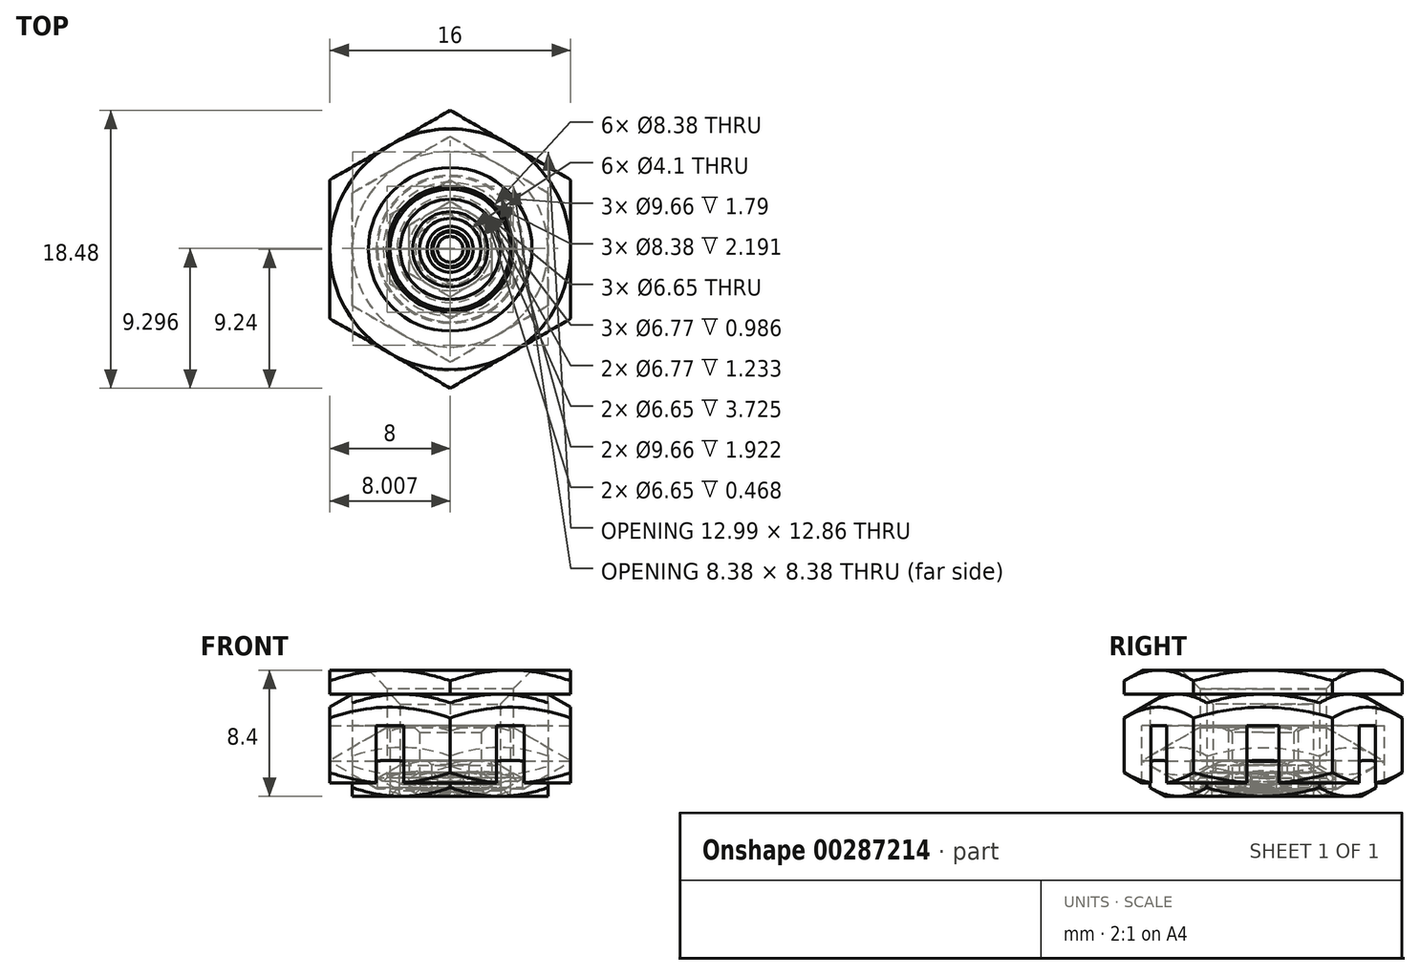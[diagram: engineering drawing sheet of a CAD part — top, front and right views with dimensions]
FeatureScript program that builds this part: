
annotation { "Feature Type Name" : "Feature", "Feature Type Description" : "" }
export const myFeature = defineFeature(function(context is Context, id is Id, definition is map)
    precondition{}
    {
        {
            var Q0;
            Q0=qCreatedBy(makeId("Top.planeOp"),FACE);
            var sketch = newSketch(context, id + "F0", { "sketchPlane" : qUnion([Q0])});
            skCircle(sketch, "E0.cCircle", {"center": v(0, 0) * mm, "radius": 8 * mm, "construction": true});
            skLineSegment(sketch, "E0.0", {"start": v(8, 4.62) * mm, "end": v(8, -4.62) * mm});
            skLineSegment(sketch, "E0.1", {"start": v(8, -4.62) * mm, "end": v(0, -9.24) * mm});
            skLineSegment(sketch, "E0.2", {"start": v(0, -9.24) * mm, "end": v(-8, -4.62) * mm});
            skLineSegment(sketch, "E0.3", {"start": v(-8, -4.62) * mm, "end": v(-8, 4.62) * mm});
            skLineSegment(sketch, "E0.4", {"start": v(-8, 4.62) * mm, "end": v(0, 9.24) * mm});
            skLineSegment(sketch, "E0.5", {"start": v(0, 9.24) * mm, "end": v(8, 4.62) * mm});
            skPoint(sketch, "E0.0.midPoint", {"position": v(8, 0) * mm});
            skCircle(sketch, "E1", {"center": v(0, 0) * mm, "radius": 4.19 * mm});
            skSolve(sketch);
        }
        {
            var Q0;
            Q0=qSketchRegion(id+"F0",true);
            extrude(context, id + "F1", {"entities" : qUnion([Q0]), "depth" : 8.4 * mm});
        }
        {
            var Q0;
            Q0=qCreatedBy(makeId("Front.planeOp"),FACE);
            var sketch = newSketch(context, id + "F2", { "sketchPlane" : qUnion([Q0])});
            skLineSegment(sketch, "E2", {"start": v(0, 0) * mm, "end": v(0, 8.4) * mm, "construction": true});
            skLineSegment(sketch, "E3", {"start": v(0, 4.2) * mm, "end": v(8, 4.2) * mm, "construction": true});
            skLineSegment(sketch, "E4", {"start": v(8, 8.4) * mm, "end": v(15.27, 8.4) * mm});
            skLineSegment(sketch, "E5", {"start": v(15.27, 8.4) * mm, "end": v(15.27, 4.2) * mm});
            skLineSegment(sketch, "E6", {"start": v(15.27, 4.2) * mm, "end": v(8, 8.4) * mm});
            skLineSegment(sketch, "E7.MirrorCS", {"start": v(15.27, 0) * mm, "end": v(15.27, 4.2) * mm});
            skLineSegment(sketch, "E8.MirrorCS", {"start": v(15.27, 4.2) * mm, "end": v(8, 0) * mm});
            skLineSegment(sketch, "E9.MirrorCS", {"start": v(8, 0) * mm, "end": v(15.27, 0) * mm});
            skSolve(sketch);
        }
        {
            var Q0;
            Q0=qSketchRegion(id+"F2",true);
            var Q1;
            Q1=sQuery(id+"F2.wireOp",EDGE,"E2");
            revolve(context, id + "F3", {"operationType" : NewBodyOperationType.REMOVE, "entities" : qUnion([Q0]), "axis" : qUnion([Q1]), "revolveType" : RevolveType.FULL, "oppositeDirection" : true});
        }
        {
            var Q0;
            Q0=makeQuery(id+"F1.opExtrude","SWEPT_FACE",FACE,{"disambiguationData":[OSD([sQuery(id+"F0.wireOp",EDGE,"E1")])]});
            chamfer(context, id + "F4", {"entities" : qUnion([Q0]), "width" : 1.25 * mm, "tangentPropagation" : true});
        }
        {
            var Q0;
            Q0=qCreatedBy(makeId("Top.planeOp"),FACE);
            var sketch = newSketch(context, id + "F5", { "sketchPlane" : qUnion([Q0])});
            skCircle(sketch, "E10.cCircle", {"center": v(0, 0) * mm, "radius": 2.75 * mm, "construction": true});
            skLineSegment(sketch, "E10.0", {"start": v(2.75, 1.59) * mm, "end": v(2.75, -1.59) * mm});
            skLineSegment(sketch, "E10.1", {"start": v(2.75, -1.59) * mm, "end": v(0, -3.18) * mm});
            skLineSegment(sketch, "E10.2", {"start": v(0, -3.18) * mm, "end": v(-2.75, -1.59) * mm});
            skLineSegment(sketch, "E10.3", {"start": v(-2.75, -1.59) * mm, "end": v(-2.75, 1.59) * mm});
            skLineSegment(sketch, "E10.4", {"start": v(-2.75, 1.59) * mm, "end": v(0, 3.18) * mm});
            skLineSegment(sketch, "E10.5", {"start": v(0, 3.18) * mm, "end": v(2.75, 1.59) * mm});
            skPoint(sketch, "E10.0.midPoint", {"position": v(2.75, 0) * mm});
            skCircle(sketch, "E11", {"center": v(0, 0) * mm, "radius": 1.23 * mm});
            skSolve(sketch);
        }
        {
            var Q0;
            Q0=qSketchRegion(id+"F5",true);
            extrude(context, id + "F6", {"entities" : qUnion([Q0]), "depth" : 2.4 * mm});
        }
        {
            var Q0;
            Q0=qCreatedBy(makeId("Front.planeOp"),FACE);
            var sketch = newSketch(context, id + "F7", { "sketchPlane" : qUnion([Q0])});
            skLineSegment(sketch, "E12.0", {"start": v(2.75, 2.4) * mm, "end": v(2.75, 0) * mm, "construction": true});
            skLineSegment(sketch, "E13", {"start": v(2.75, 2.4) * mm, "end": v(4.83, 2.4) * mm});
            skLineSegment(sketch, "E14", {"start": v(4.83, 2.4) * mm, "end": v(4.83, 0) * mm});
            skLineSegment(sketch, "E15", {"start": v(4.83, 0) * mm, "end": v(2.75, 0) * mm});
            skLineSegment(sketch, "E16", {"start": v(2.75, 2.4) * mm, "end": v(4.83, 1.2) * mm});
            skLineSegment(sketch, "E17", {"start": v(4.83, 1.2) * mm, "end": v(2.75, 0) * mm});
            skLineSegment(sketch, "E18", {"start": v(0, 0) * mm, "end": v(0, 2.35) * mm, "construction": true});
            skSolve(sketch);
        }
        {
            var Q0;
            Q0=qSketchRegion(id+"F7",true);
            var Q1;
            Q1=sQuery(id+"F7.wireOp",EDGE,"E18");
            revolve(context, id + "F8", {"operationType" : NewBodyOperationType.REMOVE, "entities" : qUnion([Q0]), "axis" : qUnion([Q1]), "revolveType" : RevolveType.FULL, "oppositeDirection" : true});
        }
        {
            var Q0;
            Q0=makeQuery(id+"F6.opExtrude","SWEPT_FACE",FACE,{"disambiguationData":[OSD([sQuery(id+"F5.wireOp",EDGE,"E11")])]});
            chamfer(context, id + "F9", {"entities" : qUnion([Q0]), "width" : 0.3 * mm, "tangentPropagation" : true});
        }
        {
            var Q0;
            Q0=qCreatedBy(makeId("Top.planeOp"),FACE);
            var sketch = newSketch(context, id + "F10", { "sketchPlane" : qUnion([Q0])});
            skCircle(sketch, "E19.cCircle", {"center": v(0, 0) * mm, "radius": 4 * mm, "construction": true});
            skLineSegment(sketch, "E19.0", {"start": v(4, 2.3) * mm, "end": v(4, -2.3) * mm});
            skLineSegment(sketch, "E19.1", {"start": v(4, -2.3) * mm, "end": v(0, -4.62) * mm});
            skLineSegment(sketch, "E19.2", {"start": v(0, -4.62) * mm, "end": v(-4, -2.3) * mm});
            skLineSegment(sketch, "E19.3", {"start": v(-4, -2.3) * mm, "end": v(-4, 2.3) * mm});
            skLineSegment(sketch, "E19.4", {"start": v(-4, 2.3) * mm, "end": v(0, 4.62) * mm});
            skLineSegment(sketch, "E19.5", {"start": v(0, 4.62) * mm, "end": v(4, 2.3) * mm});
            skPoint(sketch, "E19.0.midPoint", {"position": v(4, 0) * mm});
            skCircle(sketch, "E20", {"center": v(0, 0) * mm, "radius": 2.05 * mm});
            skSolve(sketch);
        }
        {
            var Q0;
            Q0=qSketchRegion(id+"F10",true);
            extrude(context, id + "F11", {"entities" : qUnion([Q0]), "depth" : 4.7 * mm});
        }
        {
            var Q0;
            Q0=qCreatedBy(makeId("Front.planeOp"),FACE);
            var sketch = newSketch(context, id + "F12", { "sketchPlane" : qUnion([Q0])});
            skLineSegment(sketch, "E21.0", {"start": v(-4, 4.7) * mm, "end": v(-4, 0) * mm, "construction": true});
            skLineSegment(sketch, "E22", {"start": v(-4, 4.7) * mm, "end": v(-8.07, 4.7) * mm});
            skLineSegment(sketch, "E23", {"start": v(-8.07, 4.7) * mm, "end": v(-8.07, 0) * mm});
            skLineSegment(sketch, "E24", {"start": v(-8.07, 0) * mm, "end": v(-4, 0) * mm});
            skLineSegment(sketch, "E25", {"start": v(-4, 0) * mm, "end": v(-8.07, 2.35) * mm});
            skLineSegment(sketch, "E26", {"start": v(-8.07, 2.35) * mm, "end": v(-4, 4.7) * mm});
            skLineSegment(sketch, "E27", {"start": v(0, 0) * mm, "end": v(0, 9.38) * mm, "construction": true});
            skSolve(sketch);
        }
        {
            var Q0;
            Q0=qSketchRegion(id+"F12",true);
            var Q1;
            Q1=sQuery(id+"F12.wireOp",EDGE,"E27");
            revolve(context, id + "F13", {"operationType" : NewBodyOperationType.REMOVE, "entities" : qUnion([Q0]), "axis" : qUnion([Q1]), "revolveType" : RevolveType.FULL, "oppositeDirection" : true});
        }
        {
            var Q0;
            Q0=makeQuery(id+"F11.opExtrude","SWEPT_FACE",FACE,{"disambiguationData":[OSD([sQuery(id+"F10.wireOp",EDGE,"E20")])]});
            chamfer(context, id + "F14", {"entities" : qUnion([Q0]), "width" : 0.45 * mm, "tangentPropagation" : true});
        }
        {
            var Q0;
            Q0=qCreatedBy(makeId("Top.planeOp"),FACE);
            var sketch = newSketch(context, id + "F15", { "sketchPlane" : qUnion([Q0])});
            skCircle(sketch, "E28.cCircle", {"center": v(0, 0) * mm, "radius": 6.5 * mm, "construction": true});
            skLineSegment(sketch, "E28.0", {"start": v(6.5, 3.75) * mm, "end": v(6.5, -3.75) * mm});
            skLineSegment(sketch, "E28.1", {"start": v(6.5, -3.75) * mm, "end": v(0, -7.5) * mm});
            skLineSegment(sketch, "E28.2", {"start": v(0, -7.5) * mm, "end": v(-6.5, -3.75) * mm});
            skLineSegment(sketch, "E28.3", {"start": v(-6.5, -3.75) * mm, "end": v(-6.5, 3.75) * mm});
            skLineSegment(sketch, "E28.4", {"start": v(-6.5, 3.75) * mm, "end": v(0, 7.5) * mm});
            skLineSegment(sketch, "E28.5", {"start": v(0, 7.5) * mm, "end": v(6.5, 3.75) * mm});
            skPoint(sketch, "E28.0.midPoint", {"position": v(6.5, 0) * mm});
            skCircle(sketch, "E29", {"center": v(0, 0) * mm, "radius": 3.33 * mm});
            skSolve(sketch);
        }
        {
            var Q0;
            Q0=qSketchRegion(id+"F15",true);
            extrude(context, id + "F16", {"entities" : qUnion([Q0]), "depth" : 6.8 * mm});
        }
        {
            var Q0;
            Q0=qCreatedBy(makeId("Front.planeOp"),FACE);
            var sketch = newSketch(context, id + "F17", { "sketchPlane" : qUnion([Q0])});
            skLineSegment(sketch, "E30.0", {"start": v(6.5, 6.8) * mm, "end": v(6.5, 0) * mm, "construction": true});
            skLineSegment(sketch, "E31", {"start": v(6.5, 6.8) * mm, "end": v(12.39, 6.8) * mm});
            skLineSegment(sketch, "E32", {"start": v(12.39, 6.8) * mm, "end": v(12.39, 0) * mm});
            skLineSegment(sketch, "E33", {"start": v(12.39, 0) * mm, "end": v(6.5, 0) * mm});
            skLineSegment(sketch, "E34", {"start": v(6.5, 0) * mm, "end": v(12.39, 3.4) * mm});
            skLineSegment(sketch, "E35", {"start": v(12.39, 3.4) * mm, "end": v(6.5, 6.8) * mm});
            skLineSegment(sketch, "E36", {"start": v(0, 0) * mm, "end": v(0, 12.87) * mm, "construction": true});
            skSolve(sketch);
        }
        {
            var Q0;
            Q0=qSketchRegion(id+"F17",true);
            var Q1;
            Q1=sQuery(id+"F17.wireOp",EDGE,"E36");
            revolve(context, id + "F18", {"operationType" : NewBodyOperationType.REMOVE, "entities" : qUnion([Q0]), "axis" : qUnion([Q1]), "revolveType" : RevolveType.FULL, "oppositeDirection" : true});
        }
        {
            var Q0;
            Q0=makeQuery(id+"F16.opExtrude","SWEPT_FACE",FACE,{"disambiguationData":[OSD([sQuery(id+"F15.wireOp",EDGE,"E29")])]});
            chamfer(context, id + "F19", {"entities" : qUnion([Q0]), "width" : (1.35 / 2) * mm, "tangentPropagation" : true});
        }
        {
            var Q0;
            Q0=qCreatedBy(makeId("Top.planeOp"),FACE);
            var sketch = newSketch(context, id + "F20", { "sketchPlane" : qUnion([Q0])});
            skCircle(sketch, "E37.cCircle", {"center": v(0, 0) * mm, "radius": 2 * mm, "construction": true});
            skLineSegment(sketch, "E37.0", {"start": v(2, 1.15) * mm, "end": v(2, -1.15) * mm});
            skLineSegment(sketch, "E37.1", {"start": v(2, -1.15) * mm, "end": v(0, -2.3) * mm});
            skLineSegment(sketch, "E37.2", {"start": v(0, -2.3) * mm, "end": v(-2, -1.15) * mm});
            skLineSegment(sketch, "E37.3", {"start": v(-2, -1.15) * mm, "end": v(-2, 1.15) * mm});
            skLineSegment(sketch, "E37.4", {"start": v(-2, 1.15) * mm, "end": v(0, 2.3) * mm});
            skLineSegment(sketch, "E37.5", {"start": v(0, 2.3) * mm, "end": v(2, 1.15) * mm});
            skPoint(sketch, "E37.0.midPoint", {"position": v(2, 0) * mm});
            skCircle(sketch, "E38", {"center": v(0, 0) * mm, "radius": 0.85 * mm});
            skSolve(sketch);
        }
        {
            var Q0;
            Q0 = qSketchRegion(id + "F20", true);
            extrude(context, id + "F21", {"entities" : qUnion([Q0]), "depth" : 1.6 * mm, "offsetDistance" : 25 * mm});
        }
        {
            var Q0;
            Q0=qCreatedBy(makeId("Front.planeOp"),FACE);
            var sketch = newSketch(context, id + "F22", { "sketchPlane" : qUnion([Q0])});
            skLineSegment(sketch, "E39", {"start": v(0, 0) * mm, "end": v(0, 1.6) * mm, "construction": true});
            skPoint(sketch, "E40.0", {"position": v(2, 1.6) * mm});
            skPoint(sketch, "E41.0", {"position": v(2, 0) * mm});
            skLineSegment(sketch, "E42", {"start": v(2, 1.6) * mm, "end": v(2, 0) * mm, "construction": true});
            skLineSegment(sketch, "E43", {"start": v(2, 1.6) * mm, "end": v(3.39, 0.8) * mm});
            skLineSegment(sketch, "E44", {"start": v(3.39, 0.8) * mm, "end": v(2, 0) * mm});
            skLineSegment(sketch, "E45", {"start": v(3.39, 0) * mm, "end": v(3.39, 1.6) * mm});
            skLineSegment(sketch, "E46", {"start": v(3.39, 1.6) * mm, "end": v(2, 1.6) * mm});
            skLineSegment(sketch, "E47", {"start": v(2, 0) * mm, "end": v(3.39, 0) * mm});
            skPoint(sketch, "E48", {"position": v(3.39, 0.8) * mm});
            skSolve(sketch);
        }
        {
            var Q0;
            Q0 = qSketchRegion(id + "F22", true);
            var Q1;
            Q1=sQuery(id+"F22.wireOp",EDGE,"E39");
            revolve(context, id + "F23", {"operationType" : NewBodyOperationType.REMOVE, "surfaceOperationType" : NewSurfaceOperationType.NEW, "entities" : qUnion([Q0]), "axis" : qUnion([Q1]), "revolveType" : RevolveType.FULL, "oppositeDirection" : true});
        }
        {
            var Q0;
            Q0=makeQuery(id+"F21.opExtrude","CAP_EDGE",EDGE,{"disambiguationData":[OSD([sQuery(id+"F20.wireOp",EDGE,"E38")])],"isStart":false});
            var Q1;
            Q1=makeQuery(id+"F21.opExtrude","CAP_EDGE",EDGE,{"disambiguationData":[OSD([sQuery(id+"F20.wireOp",EDGE,"E38")])],"isStart":true});
            chamfer(context, id + "F24", {"entities" : qUnion([Q0, Q1]), "width" : 0.3 * mm, "tangentPropagation" : true});
        }
    });
